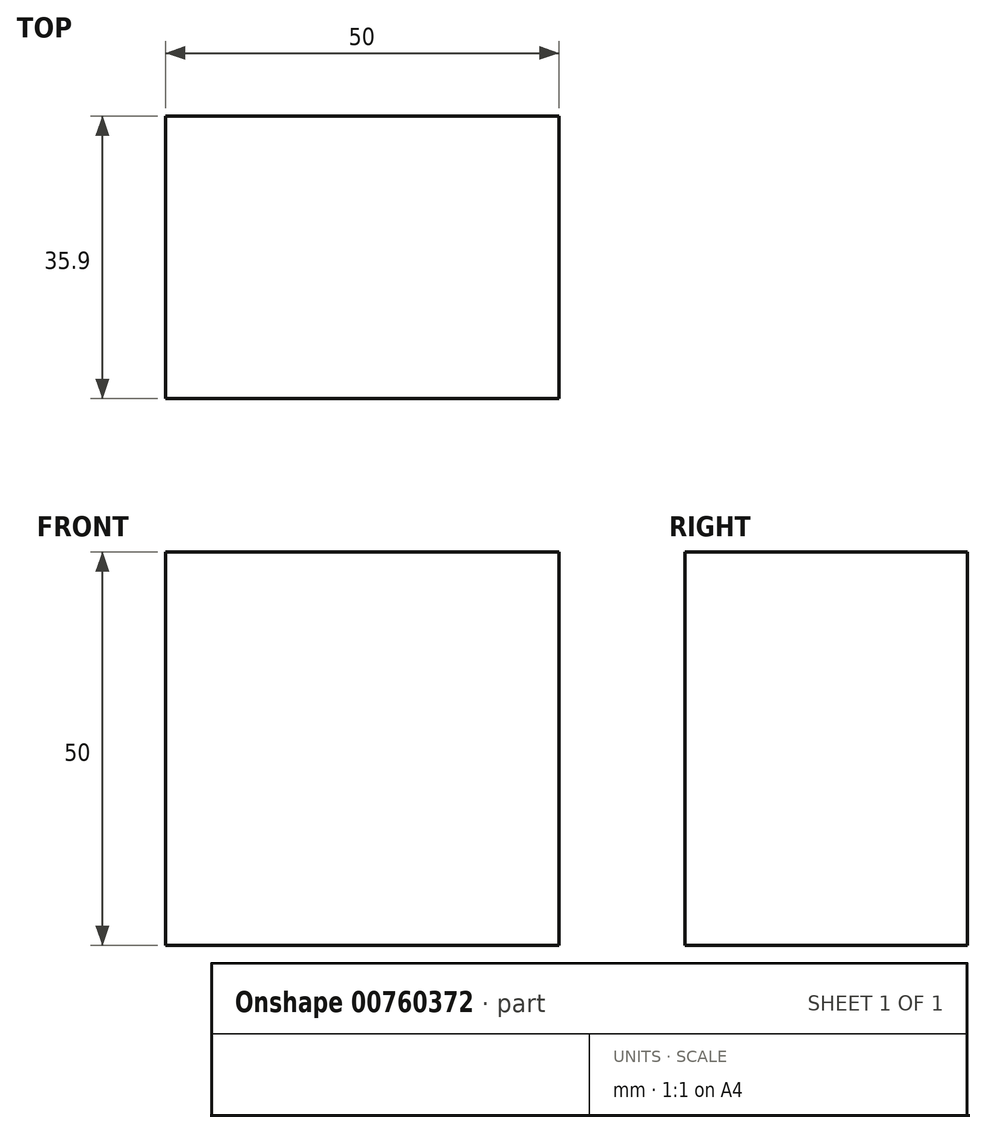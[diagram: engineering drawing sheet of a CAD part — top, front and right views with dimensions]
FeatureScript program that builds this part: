
annotation { "Feature Type Name" : "Feature", "Feature Type Description" : "" }
export const myFeature = defineFeature(function(context is Context, id is Id, definition is map)
    precondition{}
    {
        {
            var Q0;
            Q0=qCreatedBy(makeId("Front.planeOp"),FACE);
            var sketch = newSketch(context, id + "F0", { "sketchPlane" : qUnion([Q0])});
            skLineSegment(sketch, "E0.bottom", {"start": v(-25, 25) * mm, "end": v(25, 25) * mm});
            skLineSegment(sketch, "E0.top", {"start": v(-25, -25) * mm, "end": v(25, -25) * mm});
            skLineSegment(sketch, "E0.left", {"start": v(-25, 25) * mm, "end": v(-25, -25) * mm});
            skLineSegment(sketch, "E0.right", {"start": v(25, 25) * mm, "end": v(25, -25) * mm});
            skSolve(sketch);
        }
        {
            var Q0;
            Q0=makeQuery(id+"F0.imprint","IMPRINT",FACE,{"disambiguationData":[TD([[makeQuery(id+"F0.imprint","IMPRINT",EDGE,{"derivedFrom":sQuery(id+"F0.wireOp",EDGE,"E0.bottom")}),-1.0]])]});
            extrude(context, id + "F1", {"entities" : qUnion([Q0]), "endBound" : BoundingType.SYMMETRIC, "depth" : 35.9 * mm, "offsetDistance" : 25 * mm});
        }
    });
